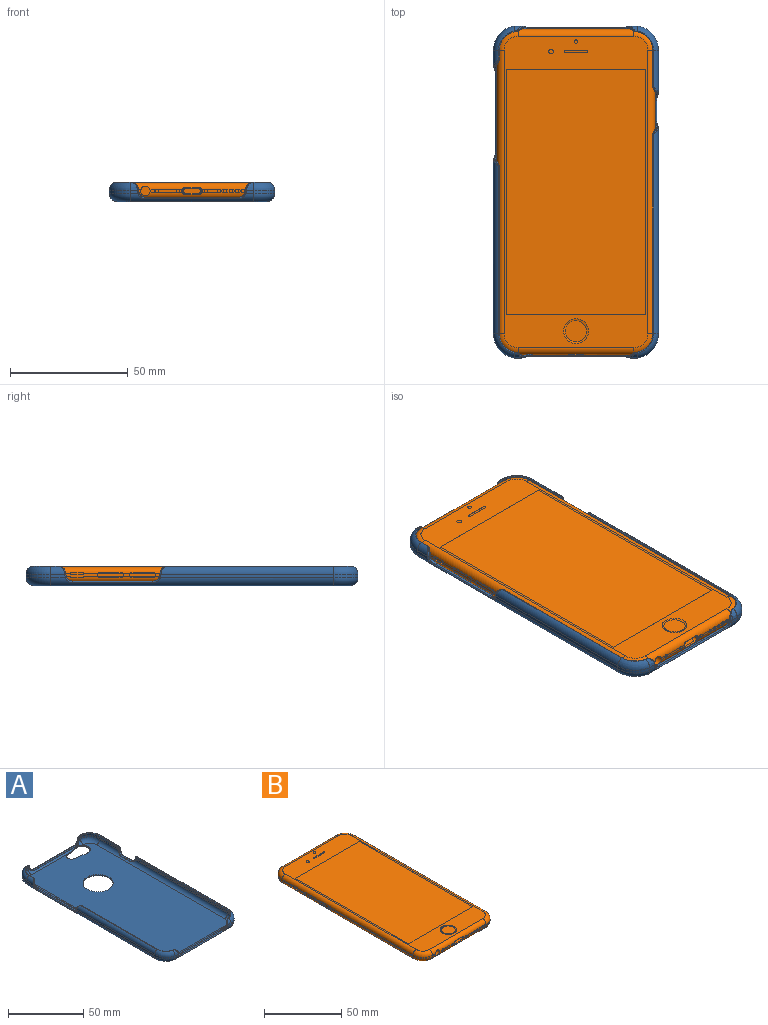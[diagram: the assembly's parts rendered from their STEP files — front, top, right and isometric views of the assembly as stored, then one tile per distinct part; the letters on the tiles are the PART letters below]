
ASSEMBLY  parts=2 mates=1
PART A: 213 faces, bbox 77.8x148.5x15.1 mm
  f0: cylinder r=3mm len=6.01mm, axis (0,1,0), area 11.1mm2, adj f1,f210,f211,f212
  f1: cylinder r=1mm len=4.25mm, axis (0,1,0), area 2mm2, adj f0,f2,f208,f209
  f2: torus R=9mm, axis (0,0,-1), area 6.1mm2, adj f1,f3,f206,f207,f212
  f3: torus R=8.27mm, axis (0,0,-1), area 6mm2, adj f2,f4,f206,f209
  f4: torus R=7mm, axis (0,0,1), area 55.5mm2, adj f3,f5,f204,f205
  f5: cylinder r=10.5mm len=10.35mm, axis (0,0,1), area 20.6mm2, adj f4,f6,f202,f203
  f6: plane 6.35x1.4mm, normal (-1,0,0), area 8.6mm2, adj f5,f7,f201,f205
  f7: torus R=3.45mm, axis (1,0,0), area 0.9mm2, adj f6,f8,f199,f200
  f8: torus R=3.05mm, axis (1,0,0), area 0mm2, adj f7,f9
  f9: bspline ~3.55x2.23mm, area 2.2mm2, adj f8,f10,f13,f205
  f10: bspline ~0.76x0.53mm, area 0.1mm2, adj f9,f11,f210
  f11: bspline ~0.37x0.3mm, area 0mm2, adj f10,f12,f205,f210
  f12: bspline ~1.69x0.86mm, area 0.5mm2, adj f11,f205,f208,f209
  f13: cylinder r=3.5mm len=2.76mm, axis (-1,0,0), area 0.8mm2, adj f9,f14,f199,f210
  f14: torus R=3.05mm, axis (1,0,0), area 0.4mm2, adj f13,f15,f210,f211
  f15: torus R=3.45mm, axis (1,0,0), area 0.3mm2, adj f14,f16,f199,f211
  f16: bspline ~3.57x3.14mm, area 2.2mm2, adj f15,f17,f198,f199
  f17: cylinder r=3mm len=120mm, axis (0,-1,0), area 450.5mm2, adj f16,f18,f194,f195,f196,f197,f198,f211
  f18: bspline ~3.94x3.14mm, area 2.2mm2, adj f17,f19,f193,f198
  f19: cylinder r=3mm len=3.01mm, axis (-1,0,0), area 5mm2, adj f18,f20,f22,f23,f192,f193
  f20: plane 33.94x1.47mm, normal (0,0,1), area 49.9mm2, adj f19,f21,f198,f199
  f21: cylinder r=0.45mm len=33.94mm, axis (0,-1,0), area 35.2mm2, adj f20,f22,f200,f201
  f22: bspline ~3.52x3.04mm, area 3.4mm2, adj f19,f21,f23,f201
  f23: torus R=3.45mm, axis (1,0,0), area 0.9mm2, adj f19,f22,f24,f191
  f24: bspline ~3.55x2.23mm, area 2.2mm2, adj f23,f25,f190,f192
  f25: bspline ~0.95x0.65mm, area 0.1mm2, adj f24,f26,f189
  f26: bspline ~3.01x2.71mm, area 2.6mm2, adj f25,f27,f28,f188,f189,f192
  f27: torus R=3.05mm, axis (1,0,0), area 0.4mm2, adj f26,f192,f193,f194
  f28: cylinder r=3mm len=73.06mm, axis (0,1,0), area 156.5mm2, adj f26,f29,f187,f194
  f29: cylinder r=1mm len=71.3mm, axis (0,1,0), area 36.7mm2, adj f28,f30,f185,f188
  f30: torus R=9mm, axis (0,0,-1), area 6.1mm2, adj f29,f31,f184,f187
  f31: bspline ~1.84x1.05mm, area 0.5mm2, adj f30,f32,f182,f183,f184
  f32: bspline ~3.44x2.59mm, area 2.2mm2, adj f31,f33,f180,f181,f182,f183
  f33: bspline ~3.07x1.95mm, area 2mm2, adj f32,f34,f179,f180,f183
  f34: torus R=3.05mm, axis (0,1,0), area 0.4mm2, adj f33,f35,f178,f180
  f35: plane 1.34x1mm, normal (0,1,0), area 1.3mm2, adj f34,f36,f37,f178,f179
  f36: cylinder r=9mm len=9mm, axis (0,0,-1), area 14.1mm2, adj f35,f187,f194,f195
  f37: cylinder r=3mm len=49mm, axis (1,0,0), area 94.3mm2, adj f35,f38,f174,f175,f176,f177,f195,f196
  f38: cylinder r=0.45mm len=39.5mm, axis (1,0,0), area 9.7mm2, adj f37,f39,f174,f177
  f39: plane 39.5x1.32mm, normal (0,0,1), area 52.2mm2, adj f38,f40,f172,f173
  f40: cylinder r=3mm len=3mm, axis (0,-1,0), area 4.3mm2, adj f39,f41,f169,f170,f171,f174
  f41: bspline ~4x3.04mm, area 3.4mm2, adj f40,f42,f169,f172
  f42: cylinder r=3.5mm len=52.5mm, axis (1,0,0), area 176.8mm2, adj f41,f43,f160,f161,f164,f167,f168,f172
  f43: plane 3.35x1.4mm, normal (0,-1,0), area 4.4mm2, adj f42,f44,f159,f169
  f44: cylinder r=10.5mm len=10.35mm, axis (0,0,1), area 20.6mm2, adj f43,f45,f158,f160
  f45: torus R=7mm, axis (0,0,1), area 55.3mm2, adj f44,f46,f157,f159
  f46: torus R=8.27mm, axis (0,0,-1), area 6.3mm2, adj f45,f47,f155,f156,f159
  f47: cylinder r=0.25mm len=83.86mm, axis (0,-1,0), area 45.6mm2, adj f46,f48,f154,f157
  f48: cylinder r=1mm len=84.8mm, axis (0,-1,0), area 43.7mm2, adj f47,f49,f153,f156
  f49: cylinder r=3mm len=86.56mm, axis (0,-1,0), area 185.8mm2, adj f48,f50,f145,f147
  f50: bspline ~3.44x2.73mm, area 2.6mm2, adj f49,f51,f52,f143,f144,f153
  f51: bspline ~0.37x0.3mm, area 0mm2, adj f50,f144,f154,f157
  f52: torus R=3.05mm, axis (1,0,0), area 0.4mm2, adj f50,f53,f143,f145
  f53: torus R=3.45mm, axis (1,0,0), area 0.3mm2, adj f52,f54,f142,f145
  f54: bspline ~3.57x3.14mm, area 2.2mm2, adj f53,f55,f141,f142
  f55: cylinder r=3mm len=120mm, axis (0,1,0), area 527.6mm2, adj f54,f56,f139,f140,f141,f145,f176,f196
  f56: bspline ~3.92x3.14mm, area 2.2mm2, adj f55,f57,f138,f141
  f57: cylinder r=3mm len=3mm, axis (1,0,0), area 5mm2, adj f56,f58,f135,f136,f137,f138
  f58: plane 8.9x1.47mm, normal (0,0,1), area 13.1mm2, adj f57,f59,f141,f142
  f59: cylinder r=0.45mm len=8.9mm, axis (0,1,0), area 9.2mm2, adj f58,f60,f134,f135
  f60: cylinder r=3.5mm len=120mm, axis (0,1,0), area 625.4mm2, adj f59,f61,f126,f127,f130,f134,f135,f158
  f61: plane 17.9x1.4mm, normal (1,0,0), area 24.8mm2, adj f60,f62,f125,f136
  f62: cylinder r=10.5mm len=10.35mm, axis (0,0,1), area 20.6mm2, adj f61,f63,f124,f126
  f63: torus R=7mm, axis (0,0,1), area 55.3mm2, adj f62,f64,f123,f125
  f64: torus R=8.27mm, axis (0,0,-1), area 6.3mm2, adj f63,f65,f121,f122,f123
  f65: cylinder r=0.25mm len=14.86mm, axis (0,-1,0), area 8.1mm2, adj f64,f66,f120,f125
  f66: bspline ~1.49x0.82mm, area 0.5mm2, adj f65,f67,f119,f125
  f67: bspline ~0.37x0.3mm, area 0mm2, adj f66,f68,f117,f125
  f68: bspline ~3.44x2.73mm, area 2.6mm2, adj f67,f69,f70,f117,f119,f137
  f69: torus R=3.05mm, axis (1,0,0), area 0.4mm2, adj f68,f137,f138,f139
  f70: cylinder r=3mm len=17.56mm, axis (0,-1,0), area 36.2mm2, adj f68,f71,f120,f139
  f71: torus R=6mm, axis (0,0,1), area 29.7mm2, adj f70,f72,f115,f116,f121
  f72: bspline ~1.89x1.62mm, area 0.5mm2, adj f71,f73,f114,f122
  f73: bspline ~3.07x1.95mm, area 2mm2, adj f72,f74,f113,f114,f115
  f74: cylinder r=3.5mm len=2.39mm, axis (0,-1,0), area 0.5mm2, adj f73,f75,f113,f114
  f75: cylinder r=3mm len=3mm, axis (0,-1,0), area 4.3mm2, adj f74,f76,f77,f110,f111,f112
  f76: torus R=3.45mm, axis (0,1,0), area 0.9mm2, adj f75,f77,f114,f124
  f77: bspline ~3.88x2.66mm, area 3.4mm2, adj f75,f76,f78,f109
  f78: cylinder r=3.5mm len=52.5mm, axis (-1,0,0), area 161mm2, adj f77,f79,f107,f108,f109,f124,f126,f161
  f79: bspline ~4x3.04mm, area 3.4mm2, adj f78,f80,f106,f109
  f80: cylinder r=3mm len=3mm, axis (0,-1,0), area 4.3mm2, adj f79,f81,f104,f105,f106,f110
  f81: cylinder r=3.5mm len=2.39mm, axis (0,-1,0), area 0.5mm2, adj f80,f82,f97,f103
  f82: torus R=3.05mm, axis (0,1,0), area 0.4mm2, adj f81,f83,f97,f104
  f83: plane 1.34x1mm, normal (0,-1,0), area 1.3mm2, adj f82,f84,f95,f96,f104
  f84: cylinder r=3mm len=49mm, axis (-1,0,0), area 81.8mm2, adj f83,f85,f86,f93,f94,f105,f111,f140
  f85: cylinder r=0.45mm len=39.5mm, axis (-1,0,0), area 9.7mm2, adj f84,f105,f110,f111
  f86: plane 10.62x1.82mm, normal (0.14,-0.99,0), area 6.3mm2, adj f84,f87,f92,f93,f107,f196
  f87: cylinder r=3.5mm len=6.93mm, axis (0,0,-1), area 6mm2, adj f86,f88,f91,f196
  f88: plane 10.29x1.48mm, normal (0.14,0.99,0), area 6.2mm2, adj f87,f89,f93,f196
  f89: cylinder r=0.8mm len=10.4mm, axis (-0.99,0.14,0), area 13.1mm2, adj f88,f90,f91,f161
  f90: torus R=5.8mm, axis (0,0,1), area 17mm2, adj f89,f93,f108,f161
  f91: torus R=4.3mm, axis (0,0,1), area 13.6mm2, adj f87,f89,f92,f161
  f92: cylinder r=0.8mm len=0.89mm, axis (0.99,0.14,0), area 0.9mm2, adj f86,f91,f107,f161
  f93: cylinder r=5mm len=10mm, axis (0,0,-1), area 10.3mm2, adj f84,f86,f88,f90,f108,f196
  f94: plane 1.34x1mm, normal (0,-1,0), area 1.3mm2, adj f84,f112,f113,f115,f116
  f95: cylinder r=9mm len=9mm, axis (0,0,1), area 14.1mm2, adj f83,f197,f211,f212
  f96: cylinder r=3mm len=1.74mm, axis (1,0,0), area 1.2mm2, adj f83,f97,f212
  f97: bspline ~3.15x2.08mm, area 2mm2, adj f81,f82,f96,f98,f102
  f98: bspline ~0.83x0.6mm, area 0.1mm2, adj f97,f99,f103
  f99: bspline ~0.56x0.48mm, area 0.1mm2, adj f98,f100,f102,f103
  f100: bspline ~0.73x0.67mm, area 0.1mm2, adj f99,f101,f102,f204
  f101: bspline ~1.2x0.83mm, area 0.4mm2, adj f100,f204,f206,f207
  f102: bspline ~1.89x1.62mm, area 0.4mm2, adj f97,f99,f100,f207,f212
  f103: bspline ~3.24x1.99mm, area 2.1mm2, adj f81,f98,f99,f106,f204
  f104: torus R=3.45mm, axis (0,1,0), area 0.3mm2, adj f80,f82,f83,f105
  f105: bspline ~3.92x3.14mm, area 2.2mm2, adj f80,f84,f85,f104
  f106: torus R=3.45mm, axis (0,1,0), area 0.9mm2, adj f79,f80,f103,f203
  f107: bspline ~18.02x3.88mm, area 14.3mm2, adj f78,f86,f92,f108
  f108: bspline ~6.52x3.14mm, area 7.3mm2, adj f78,f90,f93,f107
  f109: cylinder r=0.45mm len=39.5mm, axis (-1,0,0), area 41mm2, adj f77,f78,f79,f110
  f110: plane 39.5x1.32mm, normal (0,0,1), area 52.2mm2, adj f75,f80,f85,f109
  f111: bspline ~3.57x3.14mm, area 2.2mm2, adj f75,f84,f85,f112
  f112: torus R=3.45mm, axis (0,1,0), area 0.3mm2, adj f75,f94,f111,f113
  f113: torus R=3.05mm, axis (0,1,0), area 0.4mm2, adj f73,f74,f94,f112
  f114: bspline ~3.44x2.59mm, area 2.2mm2, adj f72,f73,f74,f76,f122,f123
  f115: cylinder r=3mm len=1.74mm, axis (1,0,0), area 1.2mm2, adj f71,f73,f94
  f116: cylinder r=9mm len=9mm, axis (0,0,-1), area 14.1mm2, adj f71,f94,f139,f140
  f117: bspline ~0.8x0.56mm, area 0.1mm2, adj f67,f68,f118
  f118: bspline ~3.55x2.23mm, area 2.2mm2, adj f117,f125,f136,f137
  f119: bspline ~1.98x1.13mm, area 0.4mm2, adj f66,f68,f120
  f120: cylinder r=1mm len=15.8mm, axis (0,-1,0), area 7.9mm2, adj f65,f70,f119,f121
  f121: torus R=9mm, axis (0,0,-1), area 6.1mm2, adj f64,f71,f120,f122
  f122: bspline ~1.84x1.05mm, area 0.5mm2, adj f64,f72,f114,f121,f123
  f123: extruded ~3.23x3.05mm, area 9.9mm2, adj f63,f64,f114,f122,f124
  f124: plane 3.35x1.4mm, normal (0,1,0), area 4.4mm2, adj f62,f76,f78,f123
  f125: cylinder r=3.5mm len=17.6mm, axis (0,-1,0), area 69.4mm2, adj f61,f63,f65,f66,f67,f118
  f126: torus R=7mm, axis (0,0,1), area 70.3mm2, adj f60,f62,f78,f161
  f127: plane 11.52x7.75mm, normal (-1,0,0), area 6.4mm2, adj f60,f128
  f128: torus R=3.05mm, axis (1,0,0), area 0mm2, adj f127,f129,f130,f158
  f129: plane 12.2x9.15mm, normal (-1,0,0), area 14.6mm2, adj f128,f157
  f130: plane 7.5x6.74mm, normal (1,0,0), area 0.3mm2, adj f60,f128,f131
  f131: torus R=3.45mm, axis (1,0,0), area 0.9mm2, adj f130,f132,f134,f142
  f132: torus R=3.05mm, axis (1,0,0), area 0mm2, adj f131,f133
  f133: bspline ~3.55x2.23mm, area 2.2mm2, adj f132,f143,f144,f157
  f134: bspline ~4x3.04mm, area 3.4mm2, adj f59,f60,f131,f142
  f135: bspline ~4x3.04mm, area 3.4mm2, adj f57,f59,f60,f136
  f136: torus R=3.45mm, axis (1,0,0), area 0.9mm2, adj f57,f61,f118,f135
  f137: cylinder r=3.5mm len=2.76mm, axis (1,0,0), area 0.8mm2, adj f57,f68,f69,f118
  f138: torus R=3.45mm, axis (1,0,0), area 0.3mm2, adj f56,f57,f69,f139
  f139: plane 17.64x1mm, normal (-1,0,0), area 17.6mm2, adj f55,f69,f70,f116,f138
  f140: torus R=6mm, axis (0,0,1), area 58.6mm2, adj f55,f84,f116,f196
  f141: cylinder r=0.45mm len=8.9mm, axis (0,1,0), area 2.2mm2, adj f54,f55,f56,f58
  f142: cylinder r=3mm len=3mm, axis (1,0,0), area 5mm2, adj f53,f54,f58,f131,f134,f143
  f143: cylinder r=3.5mm len=7mm, axis (1,0,0), area 4.1mm2, adj f50,f52,f133,f142
  f144: bspline ~0.76x0.53mm, area 0.1mm2, adj f50,f51,f133
  f145: plane 86.64x1mm, normal (-1,0,0), area 86.6mm2, adj f49,f52,f53,f55,f146
  f146: cylinder r=9mm len=9mm, axis (0,0,1), area 14.1mm2, adj f145,f147,f175,f176
  f147: torus R=6mm, axis (0,0,1), area 29.7mm2, adj f49,f146,f148,f152,f156
  f148: cylinder r=3mm len=1.74mm, axis (-1,0,0), area 1.2mm2, adj f147,f149,f175
  f149: bspline ~3.07x1.95mm, area 2mm2, adj f148,f150,f151,f152,f170
  f150: bspline ~3.2x2.27mm, area 2.2mm2, adj f149,f152,f155,f159,f169,f170
  f151: torus R=3.05mm, axis (0,1,0), area 0.4mm2, adj f149,f170,f171,f175
  f152: bspline ~1.89x1.62mm, area 0.5mm2, adj f147,f149,f150,f155
  f153: bspline ~1.91x1.08mm, area 0.4mm2, adj f48,f50,f154
  f154: bspline ~1.69x0.86mm, area 0.5mm2, adj f47,f51,f153,f157
  f155: bspline ~1.84x1.05mm, area 0.5mm2, adj f46,f150,f152,f156,f159
  f156: torus R=9mm, axis (0,0,-1), area 6.1mm2, adj f46,f48,f147,f155
  f157: cylinder r=3.5mm len=86.6mm, axis (0,-1,0), area 352.2mm2, adj f45,f47,f51,f129,f133,f154,f158
  f158: plane 86.94x7.5mm, normal (1,0,0), area 112.9mm2, adj f44,f60,f128,f157
  f159: extruded ~3.23x3.05mm, area 9.9mm2, adj f43,f45,f46,f150,f155
  f160: torus R=7mm, axis (0,0,1), area 70.3mm2, adj f42,f44,f60,f161
  f161: plane 133.71x63mm, normal (0,0,-1), area 7827.5mm2, adj f42,f60,f78,f89,f90,f91,f92,f126
  f162: torus R=11mm, axis (0,0,1), area 102.3mm2, adj f161,f163
  f163: cylinder r=10mm len=20mm, axis (0,0,1), area 25.1mm2, adj f162,f196
  f164: torus R=7mm, axis (0,0,1), area 70.3mm2, adj f42,f161,f165,f201
  f165: cylinder r=10.5mm len=10.35mm, axis (0,0,1), area 20.6mm2, adj f164,f166,f167,f191
  f166: torus R=7mm, axis (0,0,1), area 55.3mm2, adj f165,f182,f184,f190
  f167: plane 3.35x1.4mm, normal (0,-1,0), area 4.4mm2, adj f42,f165,f181,f182
  f168: bspline ~4x3.04mm, area 3.4mm2, adj f42,f172,f173,f181
  f169: torus R=3.45mm, axis (0,1,0), area 0.9mm2, adj f40,f41,f43,f150
  f170: cylinder r=3.5mm len=2.39mm, axis (0,-1,0), area 0.5mm2, adj f40,f149,f150,f151
  f171: torus R=3.45mm, axis (0,1,0), area 0.3mm2, adj f40,f151,f174,f175
  f172: cylinder r=0.45mm len=39.5mm, axis (1,0,0), area 41mm2, adj f39,f41,f42,f168
  f173: cylinder r=3mm len=3mm, axis (0,-1,0), area 4.3mm2, adj f39,f168,f177,f178,f180,f181
  f174: bspline ~3.92x3.14mm, area 2.2mm2, adj f37,f38,f40,f171
  f175: plane 1.34x1mm, normal (0,1,0), area 1.3mm2, adj f37,f146,f148,f151,f171
  f176: torus R=6mm, axis (0,0,1), area 58.6mm2, adj f37,f55,f146,f196
  f177: bspline ~3.57x3.14mm, area 2.2mm2, adj f37,f38,f173,f178
  f178: torus R=3.45mm, axis (0,1,0), area 0.3mm2, adj f34,f35,f173,f177
  f179: cylinder r=3mm len=1.74mm, axis (-1,0,0), area 1.2mm2, adj f33,f35,f187
  f180: cylinder r=3.5mm len=2.39mm, axis (0,-1,0), area 0.5mm2, adj f32,f33,f34,f173
  f181: torus R=3.45mm, axis (0,1,0), area 0.9mm2, adj f32,f167,f168,f173
  f182: extruded ~3.23x3.05mm, area 9.9mm2, adj f31,f32,f166,f167,f184
  f183: bspline ~1.89x1.62mm, area 0.5mm2, adj f31,f32,f33,f187
  f184: torus R=8.27mm, axis (0,0,-1), area 6.3mm2, adj f30,f31,f166,f182,f185
  f185: cylinder r=0.25mm len=70.36mm, axis (0,1,0), area 38.3mm2, adj f29,f184,f186,f190
  f186: bspline ~1.69x0.86mm, area 0.5mm2, adj f185,f188,f189,f190
  f187: torus R=6mm, axis (0,0,1), area 29.7mm2, adj f28,f30,f36,f179,f183
  f188: bspline ~1.98x1.13mm, area 0.4mm2, adj f26,f29,f186
  f189: bspline ~0.37x0.3mm, area 0mm2, adj f25,f26,f186,f190
  f190: cylinder r=3.5mm len=73.1mm, axis (0,1,0), area 296.8mm2, adj f24,f166,f185,f186,f189,f191
  f191: plane 73.4x1.4mm, normal (-1,0,0), area 102.5mm2, adj f23,f165,f190,f201
  f192: cylinder r=3.5mm len=2.76mm, axis (-1,0,0), area 0.8mm2, adj f19,f24,f26,f27
  f193: torus R=3.45mm, axis (1,0,0), area 0.3mm2, adj f18,f19,f27,f194
  f194: plane 73.14x1mm, normal (1,0,0), area 73.1mm2, adj f17,f27,f28,f36,f193
  f195: torus R=6mm, axis (0,0,1), area 58.6mm2, adj f17,f36,f37,f196
  f196: plane 132x61mm, normal (0,0,1), area 7570.3mm2, adj f17,f37,f55,f84,f86,f87,f88,f93
  f197: torus R=6mm, axis (0,0,1), area 58.6mm2, adj f17,f84,f95,f196
  f198: cylinder r=0.45mm len=33.94mm, axis (0,-1,0), area 8.3mm2, adj f16,f17,f18,f20
  f199: cylinder r=3mm len=3mm, axis (-1,0,0), area 5mm2, adj f7,f13,f15,f16,f20,f200
  f200: bspline ~4x3.04mm, area 3.4mm2, adj f7,f21,f199,f201
  f201: cylinder r=3.5mm len=120mm, axis (0,-1,0), area 564mm2, adj f6,f21,f22,f161,f164,f191,f200,f202
  f202: torus R=7mm, axis (0,0,1), area 70.3mm2, adj f5,f78,f161,f201
  f203: plane 3.35x1.4mm, normal (0,1,0), area 4.4mm2, adj f5,f78,f106,f204
  f204: extruded ~3.23x3.05mm, area 9.6mm2, adj f4,f100,f101,f103,f203,f206
  f205: cylinder r=3.5mm len=6.05mm, axis (0,1,0), area 22.1mm2, adj f4,f6,f9,f11,f12,f209
  f206: bspline ~0.64x0.46mm, area 0.3mm2, adj f2,f3,f101,f204
  f207: bspline ~1.54x1.04mm, area 0.2mm2, adj f2,f101,f102
  f208: bspline ~1.91x1.08mm, area 0.4mm2, adj f1,f12,f210
  f209: cylinder r=0.25mm len=3.31mm, axis (0,1,0), area 1.8mm2, adj f1,f3,f12,f205
  f210: bspline ~3.44x2.73mm, area 2.6mm2, adj f0,f10,f11,f13,f14,f208
  f211: plane 6.09x1mm, normal (1,0,0), area 6mm2, adj f0,f14,f15,f17,f95
  f212: torus R=6mm, axis (0,0,1), area 29.7mm2, adj f0,f2,f95,f96,f102
PART B: 202 faces, bbox 68.5x139.5x8 mm
  f0: plane 5.54x1.54mm, normal (-1,0,0), area 5.5mm2, adj f160,f161,f162,f163,f164,f166,f167,f168
  f1: plane 8.5x1mm, normal (-1,0,0), area 8.5mm2, adj f13,f14,f50,f160
  f2: plane 8.9x0.11mm, normal (0,0,1), area 1mm2, adj f6,f7,f14,f171
  f3: plane 11x1mm, normal (1,0,0), area 10.9mm2, adj f149,f150,f158,f159
  f4: cylinder r=1.05mm len=2.1mm, axis (-1,0,0), area 0.3mm2, adj f12,f13,f14,f152,f153,f180,f182,f184
  f5: cylinder r=1.05mm len=2.1mm, axis (-1,0,0), area 0.3mm2, adj f11,f13,f14,f152,f153,f181,f183,f185
  f6: cylinder r=1.05mm len=2.1mm, axis (-1,0,0), area 0.3mm2, adj f2,f8,f11,f13,f14,f172,f174,f176
  f7: cylinder r=1.05mm len=2.1mm, axis (-1,0,0), area 0.3mm2, adj f2,f8,f13,f14,f36,f173,f175,f177
  f8: plane 8.9x0.11mm, normal (0,0,-1), area 1mm2, adj f6,f7,f13,f178
  f9: plane 10.9x1mm, normal (-1,0,0), area 10.8mm2, adj f156,f157,f182,f183
  f10: plane 10.9x1mm, normal (-1,0,0), area 10.8mm2, adj f154,f155,f174,f175
  f11: plane 2.75x1mm, normal (-1,0,0), area 2.6mm2, adj f5,f6,f13,f14
  f12: plane 6.13x1mm, normal (-1,0,0), area 6mm2, adj f4,f13,f14,f164
  f13: cylinder r=3mm len=120mm, axis (0,-1,0), area 552.1mm2, adj f1,f4,f5,f6,f7,f8,f11,f12
  f14: cylinder r=3mm len=120mm, axis (0,1,0), area 552.1mm2, adj f1,f2,f4,f5,f6,f7,f11,f12
  f15: plane 20.07x1mm, normal (1,0,0), area 20mm2, adj f38,f41,f53,f190
  f16: plane 89.07x1mm, normal (1,0,0), area 89mm2, adj f38,f41,f44,f191
  f17: plane 1x0.26mm, normal (0,-1,0), area 0.2mm2, adj f19,f102,f103,f113
  f18: cylinder r=1.5mm len=3mm, axis (0,1,0), area 0.2mm2, adj f21,f39,f42,f100,f101,f102,f103,f104
  f19: cylinder r=1.5mm len=3mm, axis (0,1,0), area 0.2mm2, adj f17,f20,f39,f42,f100,f101,f102,f103
  f20: plane 1.28x1mm, normal (0,-1,0), area 1.1mm2, adj f19,f39,f42,f98
  f21: plane 1.28x1mm, normal (0,-1,0), area 1.1mm2, adj f18,f39,f42,f96
  f22: plane 7.82x1mm, normal (0,-1,0), area 7.6mm2, adj f39,f42,f98,f146
  f23: plane 4.32x1mm, normal (0,-1,0), area 4.1mm2, adj f39,f42,f96,f143
  f24: plane 2.19x1mm, normal (0,-1,0), area 2mm2, adj f39,f42,f80,f145
  f25: plane 1.25x1mm, normal (0,-1,0), area 1mm2, adj f39,f42,f138,f140
  f26: plane 1.25x1mm, normal (0,-1,0), area 1mm2, adj f39,f42,f134,f137
  f27: plane 1.25x1mm, normal (0,-1,0), area 1mm2, adj f39,f42,f130,f133
  f28: plane 1.25x1mm, normal (0,-1,0), area 1mm2, adj f39,f42,f126,f129
  f29: plane 1.25x1mm, normal (0,-1,0), area 1mm2, adj f39,f42,f120,f125
  f30: plane 2.81x1mm, normal (0,-1,0), area 2.8mm2, adj f39,f42,f47,f80
  f31: cylinder r=2mm len=4mm, axis (0,0,-1), area 1.2mm2, adj f32,f34,f78,f79
  f32: plane 4x2mm, normal (0,0,-1), area 6.3mm2, adj f31,f78
  f33: plane 132x61mm, normal (0,0,1), area 1783.8mm2, adj f14,f40,f41,f42,f43,f46,f49,f52
  f34: plane 132x61mm, normal (0,0,-1), area 7654.1mm2, adj f13,f31,f37,f38,f39,f45,f48,f51
  f35: plane 49x1mm, normal (0,1,0), area 49mm2, adj f37,f40,f50,f53
  f36: plane 75.63x1mm, normal (-1,0,0), area 75.5mm2, adj f7,f13,f14,f47
  f37: cylinder r=3mm len=49mm, axis (-1,0,0), area 230.9mm2, adj f34,f35,f51,f54
  f38: cylinder r=3mm len=120mm, axis (0,1,0), area 559.6mm2, adj f15,f16,f34,f45,f54,f192,f193,f194
  f39: cylinder r=3mm len=49mm, axis (1,0,0), area 217.3mm2, adj f18,f19,f20,f21,f22,f23,f24,f25
  f40: cylinder r=3mm len=49mm, axis (1,0,0), area 230.9mm2, adj f33,f35,f49,f52
  f41: cylinder r=3mm len=120mm, axis (0,-1,0), area 559.6mm2, adj f15,f16,f33,f43,f52,f187,f188,f189
  f42: cylinder r=3mm len=49mm, axis (-1,0,0), area 217.2mm2, adj f18,f19,f20,f21,f22,f23,f24,f25
  f43: torus R=6mm, axis (0,0,1), area 58.5mm2, adj f33,f41,f42,f44,f123
  f44: cylinder r=9mm len=9mm, axis (0,0,1), area 13.9mm2, adj f16,f43,f45,f121
  f45: torus R=6mm, axis (0,0,1), area 58.5mm2, adj f34,f38,f39,f44,f119
  f46: torus R=6mm, axis (0,0,1), area 58.6mm2, adj f14,f33,f42,f47
  f47: cylinder r=9mm len=9mm, axis (0,0,-1), area 14.1mm2, adj f30,f36,f46,f48
  f48: torus R=6mm, axis (0,0,1), area 58.6mm2, adj f13,f34,f39,f47
  f49: torus R=6mm, axis (0,0,1), area 58.6mm2, adj f14,f33,f40,f50
  f50: cylinder r=9mm len=9mm, axis (0,0,1), area 14.1mm2, adj f1,f35,f49,f51
  f51: torus R=6mm, axis (0,0,1), area 58.6mm2, adj f13,f34,f37,f50
  f52: torus R=6mm, axis (0,0,1), area 58.6mm2, adj f33,f40,f41,f53
  f53: cylinder r=9mm len=9mm, axis (0,0,-1), area 14.1mm2, adj f15,f35,f52,f54
  f54: torus R=6mm, axis (0,0,1), area 58.6mm2, adj f34,f37,f38,f53
  f55: plane 104x0.01mm, normal (-1,0,0), area 1mm2, adj f33,f56,f58,f59
  f56: plane 59x0.01mm, normal (0,-1,0), area 0.6mm2, adj f33,f55,f57,f59
  f57: plane 104x0.01mm, normal (1,0,0), area 1mm2, adj f33,f56,f58,f59
  f58: plane 59x0.01mm, normal (0,1,0), area 0.6mm2, adj f33,f55,f57,f59
  f59: plane 104x59mm, normal (0,0,1), area 6136mm2, adj f55,f56,f57,f58
  f60: cylinder r=0.75mm len=1.5mm, axis (0,0,1), area 0mm2, adj f33,f61
  f61: plane 1.5x1.5mm, normal (0,0,1), area 1.8mm2, adj f60
  f62: cylinder r=1mm len=2mm, axis (0,0,1), area 0.1mm2, adj f33,f63
  f63: plane 2x2mm, normal (0,0,1), area 3.1mm2, adj f62
  f64: plane 9x0.2mm, normal (0,-1,0), area 1.8mm2, adj f33,f66,f67,f68
  f65: plane 9x0.2mm, normal (0,1,0), area 1.8mm2, adj f33,f66,f67,f68
  f66: plane 10x1mm, normal (0,0,1), area 9.8mm2, adj f64,f65,f67,f68
  f67: cylinder r=0.5mm len=1mm, axis (0,0,-1), area 0.3mm2, adj f33,f64,f65,f66
  f68: cylinder r=0.5mm len=1mm, axis (0,0,1), area 0.3mm2, adj f33,f64,f65,f66
  f69: plane 9x9mm, normal (0,0,1), area 63.6mm2, adj f70
  f70: cone r=4.5mm half-angle=75.1deg, axis (0,0,1), area 23.8mm2, adj f33,f69
  f71: cylinder r=0.75mm len=1.5mm, axis (0,0,-1), area 0.9mm2, adj f34,f72
  f72: plane 1.5x1.5mm, normal (0,0,-1), area 1.8mm2, adj f71
  f73: cylinder r=3.5mm len=7mm, axis (0,0,1), area 11mm2, adj f34,f75
  f74: plane 6x6mm, normal (0,0,-1), area 5.4mm2, adj f75,f76
  f75: cone r=3mm half-angle=45deg, axis (0,0,1), area 14.4mm2, adj f73,f74
  f76: cylinder r=2.7mm len=5.4mm, axis (0,0,-1), area 0.2mm2, adj f74,f77
  f77: plane 5.4x5.4mm, normal (0,0,-1), area 22.9mm2, adj f76
  f78: plane 4x0.01mm, normal (0,-1,0), area 0mm2, adj f31,f32,f79
  f79: plane 4x2mm, normal (0,0,-1), area 6.3mm2, adj f31,f78
  f80: cylinder r=2mm len=15mm, axis (0,-1,0), area 187.4mm2, adj f24,f30,f39,f42,f81
  f81: plane 4x4mm, normal (0,-1,0), area 12.6mm2, adj f80
  f82: cylinder r=0.75mm len=1.5mm, axis (0,-1,0), area 2.1mm2, adj f83,f118,f119,f120,f121,f122,f123
  f83: plane 1.5x1.5mm, normal (0,-1,0), area 1.8mm2, adj f82
  f84: cylinder r=0.75mm len=1.5mm, axis (0,-1,0), area 2.1mm2, adj f85,f124,f125,f126,f127
  f85: plane 1.5x1.5mm, normal (0,-1,0), area 1.8mm2, adj f84
  f86: cylinder r=0.75mm len=1.5mm, axis (0,-1,0), area 2.1mm2, adj f87,f128,f129,f130,f131
  f87: plane 1.5x1.5mm, normal (0,-1,0), area 1.8mm2, adj f86
  f88: cylinder r=0.75mm len=1.5mm, axis (0,-1,0), area 2.1mm2, adj f89,f132,f133,f134,f135
  f89: plane 1.5x1.5mm, normal (0,-1,0), area 1.8mm2, adj f88
  f90: cylinder r=0.75mm len=1.5mm, axis (0,-1,0), area 2.1mm2, adj f91,f136,f137,f138,f139
  f91: plane 1.5x1.5mm, normal (0,-1,0), area 1.8mm2, adj f90
  f92: cylinder r=0.75mm len=1.5mm, axis (0,-1,0), area 2.1mm2, adj f93,f140,f141,f142,f143
  f93: plane 1.5x1.5mm, normal (0,-1,0), area 1.8mm2, adj f92
  f94: cylinder r=0.75mm len=1.5mm, axis (0,-1,0), area 2.1mm2, adj f95,f144,f145,f146,f147
  f95: plane 1.5x1.5mm, normal (0,-1,0), area 1.8mm2, adj f94
  f96: cylinder r=0.75mm len=1.5mm, axis (0,-1,0), area 0.2mm2, adj f21,f23,f39,f42,f97
  f97: plane 1.5x1.5mm, normal (0,-1,0), area 1.8mm2, adj f96
  f98: cylinder r=0.75mm len=1.5mm, axis (0,-1,0), area 0.2mm2, adj f20,f22,f39,f42,f99
  f99: plane 1.5x1.5mm, normal (0,-1,0), area 1.8mm2, adj f98
  f100: plane 5.5x0.05mm, normal (0,0,1), area 0.3mm2, adj f18,f19,f42,f102
  f101: plane 5.5x0.05mm, normal (0,0,-1), area 0.3mm2, adj f18,f19,f39,f103
  f102: cylinder r=3.05mm len=8.33mm, axis (1,0,0), area 0.7mm2, adj f17,f18,f19,f100,f104,f115,f116,f117
  f103: cylinder r=3.05mm len=8.33mm, axis (1,0,0), area 0.7mm2, adj f17,f18,f19,f101,f104,f110,f111,f112
  f104: plane 1x0.26mm, normal (0,-1,0), area 0.2mm2, adj f18,f102,f103,f114
  f105: plane 6.58x5.5mm, normal (0,0,-1), area 36.2mm2, adj f106,f108,f109,f117
  f106: cylinder r=1mm len=6.71mm, axis (0,-1,0), area 20.9mm2, adj f105,f107,f109,f111,f113,f115
  f107: plane 6.58x5.5mm, normal (0,0,1), area 36.2mm2, adj f106,f108,f109,f110
  f108: cylinder r=1mm len=6.71mm, axis (0,-1,0), area 20.9mm2, adj f105,f107,f109,f112,f114,f116
  f109: plane 7.5x2mm, normal (0,-1,0), area 14.1mm2, adj f105,f106,f107,f108
  f110: plane 5.5x0.44mm, normal (0,-0.81,0.59), area 3mm2, adj f103,f107,f111,f112
  f111: bspline ~1.24x1.08mm, area 0.7mm2, adj f103,f106,f110,f113
  f112: bspline ~1.24x1.08mm, area 0.7mm2, adj f103,f108,f110,f114
  f113: cone r=1mm half-angle=45deg, axis (0,-1,0), area 0.4mm2, adj f17,f106,f111,f115
  f114: cone r=1mm half-angle=45deg, axis (0,-1,0), area 0.4mm2, adj f104,f108,f112,f116
  f115: bspline ~1.24x1.08mm, area 0.7mm2, adj f102,f106,f113,f117
  f116: bspline ~1.24x1.08mm, area 0.7mm2, adj f102,f108,f114,f117
  f117: plane 5.5x0.44mm, normal (0,-0.81,-0.59), area 3mm2, adj f102,f105,f115,f116
  f118: bspline ~1.12x0.44mm, area 0.1mm2, adj f39,f82,f119,f120
  f119: bspline ~0.16x0.16mm, area 0mm2, adj f45,f82,f118,f121
  f120: cone r=0.75mm half-angle=45deg, axis (0,-1,0), area 0.1mm2, adj f29,f82,f118,f122
  f121: bspline ~1x0.27mm, area 0.1mm2, adj f44,f82,f119,f123
  f122: bspline ~1.12x0.44mm, area 0.1mm2, adj f42,f82,f120,f123
  f123: bspline ~0.16x0.16mm, area 0mm2, adj f43,f82,f121,f122
  f124: bspline ~1.25x0.44mm, area 0.1mm2, adj f39,f84,f125,f126
  f125: cone r=0.75mm half-angle=45deg, axis (0,-1,0), area 0.1mm2, adj f29,f84,f124,f127
  f126: cone r=0.75mm half-angle=45deg, axis (0,-1,0), area 0.1mm2, adj f28,f84,f124,f127
  f127: bspline ~1.25x0.44mm, area 0.1mm2, adj f42,f84,f125,f126
  f128: bspline ~1.25x0.44mm, area 0.1mm2, adj f39,f86,f129,f130
  f129: cone r=0.75mm half-angle=45deg, axis (0,-1,0), area 0.1mm2, adj f28,f86,f128,f131
  f130: cone r=0.75mm half-angle=45deg, axis (0,-1,0), area 0.1mm2, adj f27,f86,f128,f131
  f131: bspline ~1.25x0.44mm, area 0.1mm2, adj f42,f86,f129,f130
  f132: bspline ~1.25x0.44mm, area 0.1mm2, adj f39,f88,f133,f134
  f133: cone r=0.75mm half-angle=45deg, axis (0,-1,0), area 0.1mm2, adj f27,f88,f132,f135
  f134: cone r=0.75mm half-angle=45deg, axis (0,-1,0), area 0.1mm2, adj f26,f88,f132,f135
  f135: bspline ~1.25x0.44mm, area 0.1mm2, adj f42,f88,f133,f134
  f136: bspline ~1.25x0.44mm, area 0.1mm2, adj f39,f90,f137,f138
  f137: cone r=0.75mm half-angle=45deg, axis (0,-1,0), area 0.1mm2, adj f26,f90,f136,f139
  f138: cone r=0.75mm half-angle=45deg, axis (0,-1,0), area 0.1mm2, adj f25,f90,f136,f139
  f139: bspline ~1.25x0.44mm, area 0.1mm2, adj f42,f90,f137,f138
  f140: cone r=0.75mm half-angle=45deg, axis (0,-1,0), area 0.1mm2, adj f25,f92,f141,f142
  f141: bspline ~1.25x0.44mm, area 0.1mm2, adj f42,f92,f140,f143
  f142: bspline ~1.25x0.44mm, area 0.1mm2, adj f39,f92,f140,f143
  f143: cone r=0.75mm half-angle=45deg, axis (0,-1,0), area 0.1mm2, adj f23,f92,f141,f142
  f144: bspline ~1.25x0.44mm, area 0.1mm2, adj f42,f94,f145,f146
  f145: cone r=0.75mm half-angle=45deg, axis (0,-1,0), area 0.1mm2, adj f24,f94,f144,f147
  f146: cone r=0.75mm half-angle=45deg, axis (0,-1,0), area 0.1mm2, adj f22,f94,f144,f147
  f147: bspline ~1.25x0.44mm, area 0.1mm2, adj f39,f94,f145,f146
  f148: plane 8.9x0.11mm, normal (0,0,1), area 1mm2, adj f149,f150,f159,f187
  f149: cylinder r=1.05mm len=2.1mm, axis (1,0,0), area 0.3mm2, adj f3,f148,f151,f158,f159,f188,f190,f192
  f150: cylinder r=1.05mm len=2.1mm, axis (1,0,0), area 0.3mm2, adj f3,f148,f151,f158,f159,f189,f191,f193
  f151: plane 8.9x0.11mm, normal (0,0,-1), area 1mm2, adj f149,f150,f158,f194
  f152: plane 8.9x0.11mm, normal (0,0,1), area 1mm2, adj f4,f5,f14,f179
  f153: plane 8.9x0.11mm, normal (0,0,-1), area 1mm2, adj f4,f5,f13,f186
  f154: cylinder r=3.15mm len=10.63mm, axis (0,-1,0), area 5mm2, adj f10,f171,f172,f173
  f155: cylinder r=3.15mm len=10.63mm, axis (0,-1,0), area 5mm2, adj f10,f176,f177,f178
  f156: cylinder r=3.15mm len=10.63mm, axis (0,-1,0), area 5mm2, adj f9,f179,f180,f181
  f157: cylinder r=3.15mm len=10.63mm, axis (0,-1,0), area 5mm2, adj f9,f184,f185,f186
  f158: cylinder r=3.15mm len=10.75mm, axis (0,-1,0), area 5.4mm2, adj f3,f149,f150,f151
  f159: cylinder r=3.15mm len=10.75mm, axis (0,-1,0), area 5.4mm2, adj f3,f148,f149,f150
  f160: plane 1x0.75mm, normal (0,-1,0), area 0.7mm2, adj f0,f1,f161,f166
  f161: cylinder r=0.5mm len=0.75mm, axis (-1,0,0), area 0.6mm2, adj f0,f13,f160,f162
  f162: plane 4.5x0.71mm, normal (0,0,1), area 3.2mm2, adj f0,f13,f161,f163
  f163: cylinder r=0.5mm len=0.75mm, axis (-1,0,0), area 0.6mm2, adj f0,f13,f162,f164
  f164: plane 1x0.75mm, normal (0,1,0), area 0.7mm2, adj f0,f12,f163,f168
  f165: plane 4.5x0.14mm, normal (0,0,1), area 0.6mm2, adj f14,f166,f169,f196
  f166: cylinder r=0.5mm len=1mm, axis (1,0,0), area 0.8mm2, adj f0,f14,f160,f165,f167,f195
  f167: plane 4.5x0.85mm, normal (0,0,-1), area 3.8mm2, adj f0,f166,f168,f197
  f168: extruded ~0.85x0.5mm, area 0.7mm2, adj f0,f164,f167,f169,f199
  f169: cylinder r=0.5mm len=0.5mm, axis (1,0,0), area 0.1mm2, adj f14,f165,f168,f198
  f170: plane 5.4x0.9mm, normal (-1,0,0), area 4.7mm2, adj f195,f196,f197,f198,f199
  f171: bspline ~14.07x0.05mm, area 0.6mm2, adj f2,f154,f172,f173
  f172: bspline ~1.24x0.75mm, area 0.1mm2, adj f6,f154,f171,f174
  f173: bspline ~1.24x0.75mm, area 0.1mm2, adj f7,f154,f171,f175
  f174: torus R=1mm, axis (-1,0,0), area 0.1mm2, adj f6,f10,f172,f176
  f175: torus R=1mm, axis (-1,0,0), area 0.1mm2, adj f7,f10,f173,f177
  f176: bspline ~1.24x0.75mm, area 0.1mm2, adj f6,f155,f174,f178
  f177: bspline ~1.24x0.75mm, area 0.1mm2, adj f7,f155,f175,f178
  f178: bspline ~17.17x0.05mm, area 0.6mm2, adj f8,f155,f176,f177
  f179: cylinder r=0.05mm len=8.9mm, axis (0,-1,0), area 0.6mm2, adj f152,f156,f180,f181
  f180: bspline ~1.24x0.75mm, area 0.1mm2, adj f4,f156,f179,f182
  f181: bspline ~1.24x0.75mm, area 0.1mm2, adj f5,f156,f179,f183
  f182: torus R=1mm, axis (-1,0,0), area 0.1mm2, adj f4,f9,f180,f184
  f183: torus R=1mm, axis (-1,0,0), area 0.1mm2, adj f5,f9,f181,f185
  f184: bspline ~1.24x0.75mm, area 0.1mm2, adj f4,f157,f182,f186
  f185: bspline ~1.24x0.75mm, area 0.1mm2, adj f5,f157,f183,f186
  f186: cylinder r=0.05mm len=8.9mm, axis (0,-1,0), area 0.6mm2, adj f153,f157,f184,f185
  f187: cylinder r=0.05mm len=8.9mm, axis (0,-1,0), area 0.6mm2, adj f41,f148,f188,f189
  f188: bspline ~1.31x0.82mm, area 0.1mm2, adj f41,f149,f187,f190
  f189: bspline ~1.31x0.82mm, area 0.1mm2, adj f41,f150,f187,f191
  f190: torus R=1.1mm, axis (1,0,0), area 0.1mm2, adj f15,f149,f188,f192
  f191: torus R=1.1mm, axis (1,0,0), area 0.1mm2, adj f16,f150,f189,f193
  f192: bspline ~1.31x0.82mm, area 0.1mm2, adj f38,f149,f190,f194
  f193: bspline ~1.25x0.66mm, area 0.1mm2, adj f38,f150,f191,f194
  f194: cylinder r=0.05mm len=8.9mm, axis (0,1,0), area 0.6mm2, adj f38,f151,f192,f193
  f195: torus R=0.45mm, axis (-1,0,0), area 0.1mm2, adj f166,f170,f196,f197
  f196: cylinder r=0.05mm len=4.5mm, axis (0,-1,0), area 0.4mm2, adj f165,f170,f195,f198
  f197: cylinder r=0.05mm len=4.5mm, axis (0,1,0), area 0.4mm2, adj f167,f170,f195,f199
  f198: torus R=0.45mm, axis (-1,0,0), area 0.1mm2, adj f169,f170,f196,f199
  f199: bspline ~0.61x0.58mm, area 0.1mm2, adj f168,f170,f197,f198
  f200: cylinder r=10mm len=20mm, axis (0,0,-1), area 0.6mm2, adj f34,f201
  f201: plane 20x20mm, normal (0,0,-1), area 314.2mm2, adj f200
PLACE A t=(37.9,20.31,-16.32)mm
PLACE B t=(37.9,20.31,-16.72)mm
MATE fastened B.f200 <-> A.f162  axis (0,0,-1) through (37.9,48.31,-16.72)mm
